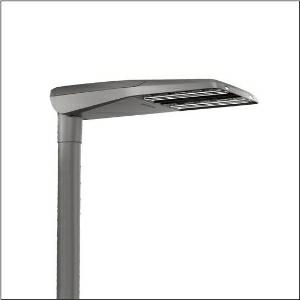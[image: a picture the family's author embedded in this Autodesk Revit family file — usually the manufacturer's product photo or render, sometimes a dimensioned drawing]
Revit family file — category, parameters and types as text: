
# Revit family: streetlight_sl_11_iq_midi___st1_0a_5xc3m51f08me_eb90
name_source: partatom
category: Lighting Fixtures
units: mm (PartAtom-declared; Revit-internal decimal feet)

## family parameters
Cut with Voids When Loaded = No
Host = Face
Light Source = No
Part Type = Normal
Room Calculation Point = No
Round Connector Dimension = Use Diameter
Shared = No

## types (1)
- --- (1 x LED, 17550 lm, 124.7 W, 3000K)
    Apparent Load = 125 VA
    CIE Flux Codes = 33 66 96 100 100
    Color Rendering = 70
    Color Temperature = 3000K
    Default Elevation = 1800 mm
    Description = Streetlight SL 11 iQ midi, mast luminaire, primary light control with 3 zone facetted reflector, of plastic, silver coated, highly specular, primary optical cover: cover, of PMMA, transparent, light distribution: ST1.0a, light emission: direct distribution, primary light characteristic: asymmetric, installation type: post-top, side-entry, lamps: LED, High Power LED, rated values: 17.550lm | 124,7W | 140,7lm/W (begin service life); end service life: 17.550lm | 132,2W; at 50% lumin. flux: 8.775lm | 57,2W | 153,4lm/W, colour temperature: 3000K, colour rendering: CRI > 70, light colour: 730, light setting 1 begin service life: 100% | 17.550lm | 124,7W | 140,7lm/W | 3.000K, light setting 1 end service life: 132,2W, further light settings possible, control: optimised constant luminous flux control (CLO 2.0), Street-Remote, Desk-Remote (wireless, voltage-free reading and setting of iQ features in the workshop via application-optimized NFC function/RFID function), Light-Fading, Smart-Wire, Night-Set, Lumen-Switch, Temp-Guard, Auto-Match, with cable H07RN-F 5x 1.5mm², mains connection: 230..240V, AC, 50/60Hz, connection cable pre-assembled, cable length: 12,5m, luminaire housing, of diecast aluminium, powder-coated, Siteco® metallic grey (DB 702S), please order mast flange separately, inclination adjustable without tools: 0°, 5°, 10°, 15° (post-top) | 0°, -5°, -10°, -15° (side-entry), sealing non-destructively replaceable, multi-level sealing system, length: 780mm, width: 376mm, height: 118mm, mast flange for spigot size: 42mm (side-entry): 5XC10008XM4, 60/48mm (side-entry/post-top): 5XC10108XM2, 76/60mm (side-entry/post-top): 5XC10108XM1, equipment: Power, protection rating (complete): IP66, insulation class (complete): insulation class II (safety insulation), certification: CE, ENEC, ENEC+, VDE, impact resistance: IK10, permissible operating ambient temperature for outdoor applications: -25..+50°C, standard-compliant lighting for roads and squares, Environmental Product Declaration (EPD) tested and certified by an independent institute, packaging unit: 1 piece

Light Distribution: ST1.0a
    Height = 118 mm
    Lamp = 1 x LED
    Lamp Light Flux = 17550 lm
    Lamp Power = 124.7 W
    Lamp count = 1
    Length = 780 mm
    Luminous efficacy = 141 lm/W
    Manufacturer = Siteco
    ModVariant = No
    Model = 5XC3M51F08ME
    Number of Poles = 1
    OnlyDefault = Yes
    Power Factor = 1
    Product Name = Streetlight SL 11 iQ midi | ST1.0a
    Product group = mast luminaire | pylon top
    ProductGroupID = 6100
    Protection Class = Protection class II
    Protection Degree = IP 66
    RLX_Detail_Level = 1
    RLX_Emergency_Light_Flux = 0 lm
    RLX_Emergency_Type = 0
    RLX_Emergency_Type_DB = No
    RlxData = <blob elided: 70373 chars, md5=17121d7b>
    Socket = socket
    Standby Power = 0 W
    System Light Flux = 17550 lm
    System Power = 125 W
    Type Comments = factory setting: luminous flux: 100 % | dim-lin: 254 | 557 mA
    Type Image = l_1005960.jpg
    URL = http://relux.com
    VarID = @adj_088490
    Voltage = 0 V
    Weight = 0.00 kg
    Width = 376 mm

## geometry (parser evidence)
native form markers: Blend x4, Sweep x12
no freeform markers — native parametric forms only
